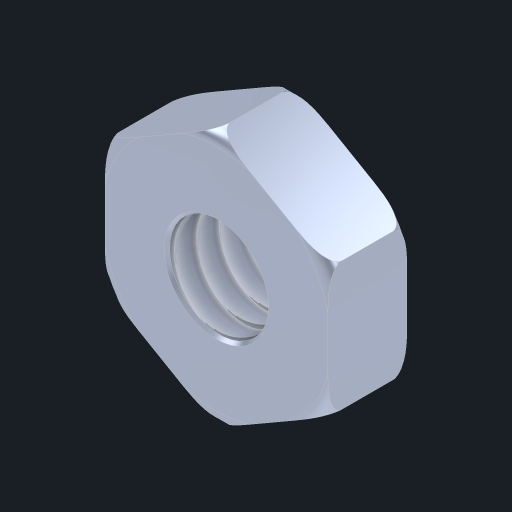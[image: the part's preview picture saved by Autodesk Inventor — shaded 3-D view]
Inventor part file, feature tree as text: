
AUTODESK INVENTOR PART (.ipt)
format: ipt  version: 2023 (Build 270158030, 158C)  size: 206,848 bytes
history: native  units: in
note: dims shown in document units (in); Inventor stores cm internally (conversion verified against a paired STEP export)
features: other x3, move_body x2, thread x1
ambient origin geometry x8: Origin, YZ Plane, XZ Plane, XY Plane, X Axis, Y Axis, Z Axis, Center Point
bodies: Solid1 (feature_tree)
feature tree (6):
  other  "Bi-directional Cylinder.ipt"
  thread  "Thread1"  [1 undecoded]
  move_body  "Move Body2"
  move_body  "Move Body3"
  other  "Solid1::Bi-directional Cylinder.ipt"
  other  "TaggingFeature1"
note: 1 required parameter value undecoded (feature->parameter linkage not recoverable at this tier; creation-order binding heuristic only, values carry confidence <= 0.55)
